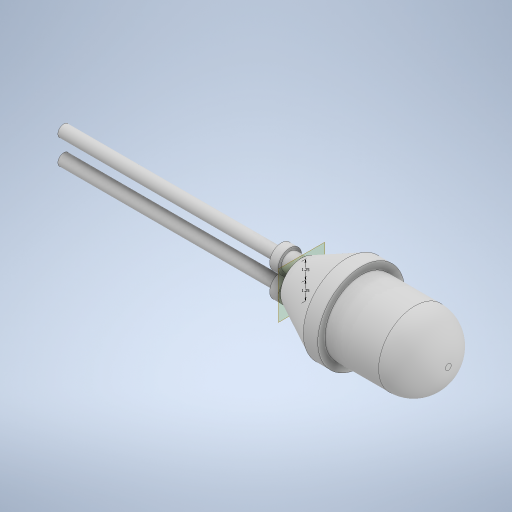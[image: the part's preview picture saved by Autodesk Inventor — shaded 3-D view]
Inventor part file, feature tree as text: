
AUTODESK INVENTOR PART (.ipt)
format: ipt  version: 2024 (Build 280153000, 153)  size: 335,872 bytes
history: native  units: in
note: dims shown in document units (in); Inventor stores cm internally (conversion verified against a paired STEP export)
features: sketch x4, revolve x2, plane x1, mirror x1
ambient origin geometry x8: Origin, YZ Plane, XZ Plane, XY Plane, X Axis, Y Axis, Z Axis, Center Point
bodies: Solid1 (feature_tree)
feature tree (8):
  revolve  "Revolution1"  [1 undecoded]
  plane  "Work Plane1"
  sketch  "Sketch2"  dims[d14=0.3937in d17=0.5906in]
  sketch  "Sketch3"  dims[d23=0.0236in]
  revolve  "Revolution2"  [1 undecoded]
  mirror  "Mirror1"
  sketch  "Sketch1"  dims[d8=0.1181in d13=0.0906in]
  sketch  "Sketch4"  dims[d24=0.0079in d25=0.0315in d26=0.0315in d27=0.5906in d28=0.0157in d29=0.0236in d30=0.0079in d31=0.0787in d32=0.0157in d33=0.1181in d34=0.0394in d35=90.0deg d36=0.0in d39=0.0492in d40=0.0492in d41=0.0315in d42=0.0079in d43=0.0236in d44=0.0157in d45=0.5906in d46=0.0315in d47=0.5906in d48=0.0157in d49=0.0236in d50=0.0079in d51=0.0315in d52=90.0deg]
note: 2 required parameter values undecoded (feature->parameter linkage not recoverable at this tier; creation-order binding heuristic only, values carry confidence <= 0.55)
